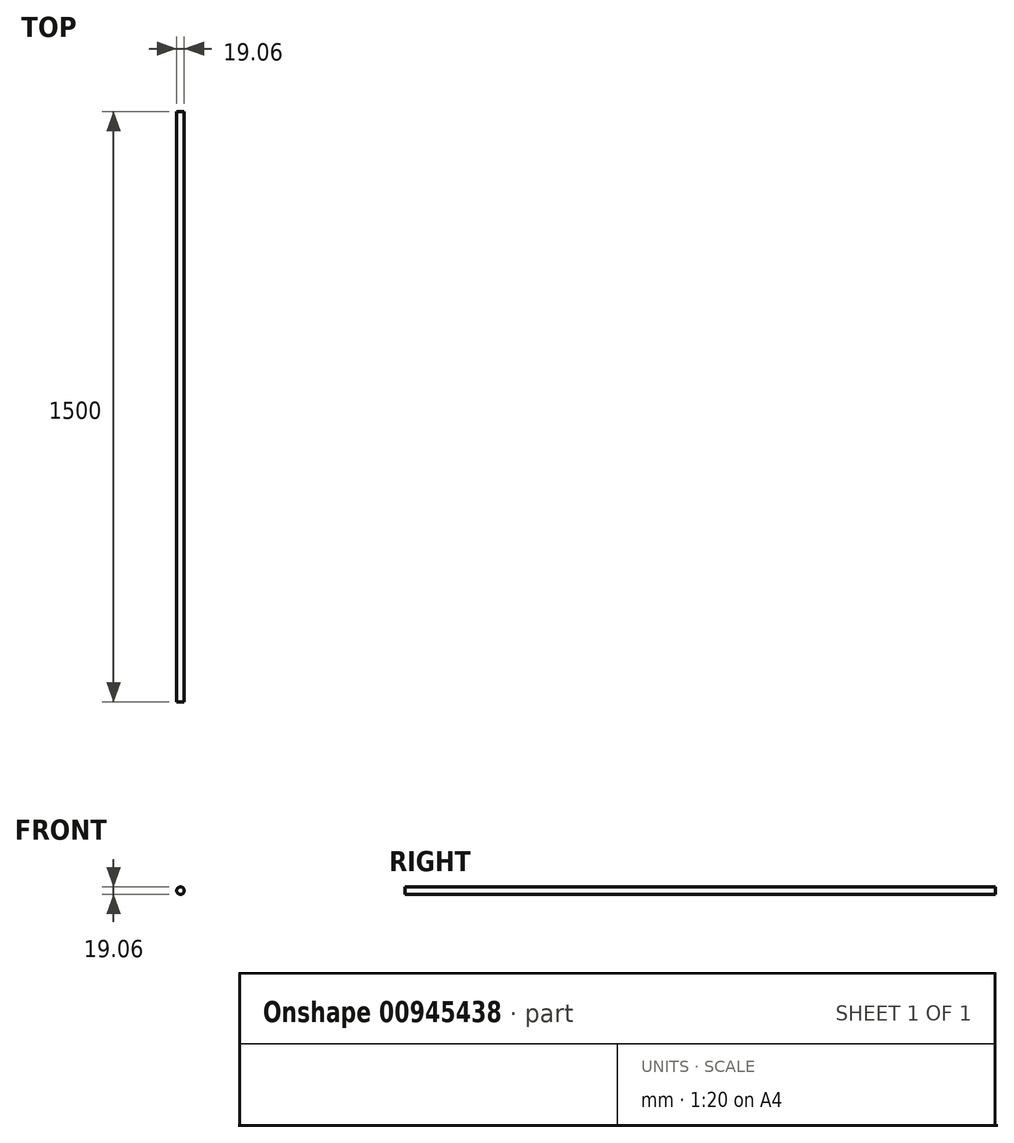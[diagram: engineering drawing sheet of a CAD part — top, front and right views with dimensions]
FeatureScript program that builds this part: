
annotation { "Feature Type Name" : "Feature", "Feature Type Description" : "" }
export const myFeature = defineFeature(function(context is Context, id is Id, definition is map)
    precondition{}
    {
        {
            var Q0;
            Q0=qCreatedBy(makeId("Front.planeOp"),FACE);
            var sketch = newSketch(context, id + "F0", { "sketchPlane" : qUnion([Q0])});
            skCircle(sketch, "E0", {"center": v(0, 0) * mm, "radius": 9.53 * mm});
            skSolve(sketch);
        }
        {
            var Q0;
            Q0=sQuery(id+"F0.wireOp",EDGE,"sJJWTbRt-4jci-nDqK-0AGt-oJkoLYQSoBqF");
            var Q1;
            Q1=sQuery(id+"F0.wireOp",EDGE,"E0");
            extrude(context, id + "F1", {"bodyType" : ToolBodyType.SURFACE, "surfaceEntities" : qUnion([Q0, Q1]), "depth" : 1500 * mm, "offsetDistance" : 25.4 * mm});
        }
    });
